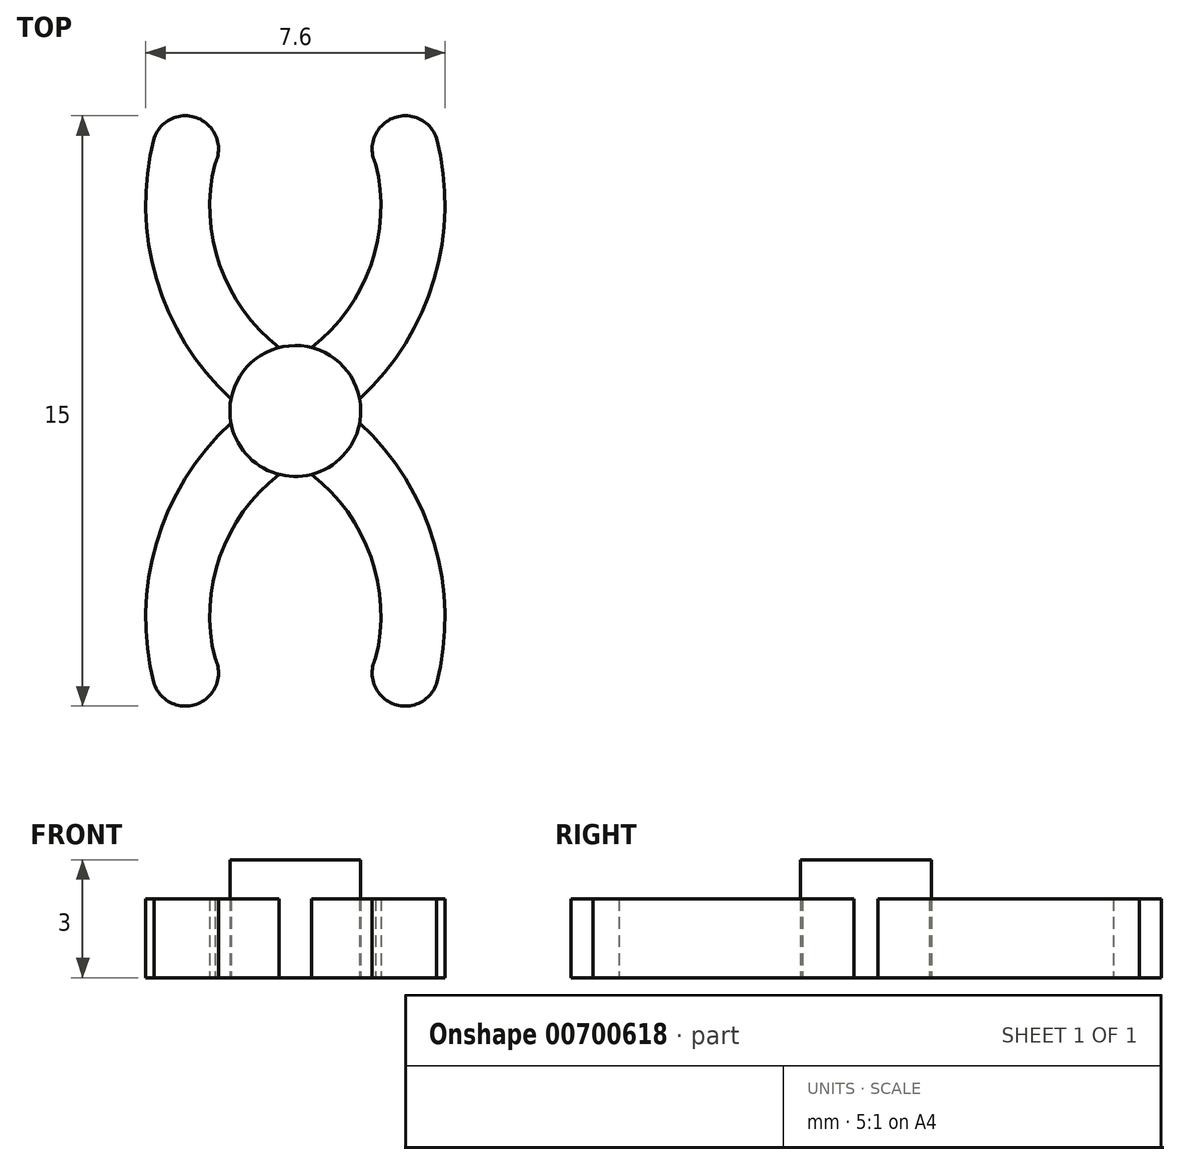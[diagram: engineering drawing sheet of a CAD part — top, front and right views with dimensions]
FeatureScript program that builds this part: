
annotation { "Feature Type Name" : "Feature", "Feature Type Description" : "" }
export const myFeature = defineFeature(function(context is Context, id is Id, definition is map)
    precondition{}
    {
        {
            var Q0;
            Q0=qCreatedBy(makeId("Top.planeOp"),FACE);
            var sketch = newSketch(context, id + "F0", { "sketchPlane" : qUnion([Q0])});
            skLineSegment(sketch, "E0", {"start": v(-1.04, 1.33) * mm, "end": v(-1.04, -7.3) * mm, "construction": true});
            skArc(sketch, "E1", {"start": v(-1.04, 1.33) * mm, "mid": v(0.79, 3.47) * mm, "end": v(1, 6.28) * mm});
            skLineSegment(sketch, "E2", {"start": v(1, 6.28) * mm, "end": v(6, 6.28) * mm, "construction": true});
            skLineSegment(sketch, "E3", {"start": v(1, 6.28) * mm, "end": v(4.09, 7.6) * mm, "construction": true});
            skArc(sketch, "E4", {"start": v(2.54, 6.94) * mm, "mid": v(1.42, 7.43) * mm, "end": v(1, 6.28) * mm});
            skArc(sketch, "E5", {"start": v(0.24, 0) * mm, "mid": v(2.42, 3.13) * mm, "end": v(2.54, 6.94) * mm});
            skArc(sketch, "E6.MirrorCS", {"start": v(-1.04, -1.33) * mm, "mid": v(0.79, -3.47) * mm, "end": v(1, -6.28) * mm});
            skArc(sketch, "E7.MirrorCS", {"start": v(2.54, -6.94) * mm, "mid": v(1.42, -7.43) * mm, "end": v(1, -6.28) * mm});
            skArc(sketch, "E8.MirrorCS", {"start": v(0.24, 0) * mm, "mid": v(2.42, -3.13) * mm, "end": v(2.54, -6.94) * mm});
            skArc(sketch, "E9.MirrorCS", {"start": v(-1.04, -1.33) * mm, "mid": v(-2.87, -3.47) * mm, "end": v(-3.08, -6.28) * mm});
            skArc(sketch, "E10.MirrorCS", {"start": v(-1.04, 1.33) * mm, "mid": v(-2.87, 3.47) * mm, "end": v(-3.08, 6.28) * mm});
            skArc(sketch, "E11.MirrorCS", {"start": v(-2.32, 0) * mm, "mid": v(-4.5, -3.13) * mm, "end": v(-4.63, -6.94) * mm});
            skArc(sketch, "E12.MirrorCS", {"start": v(-2.32, 0) * mm, "mid": v(-4.5, 3.13) * mm, "end": v(-4.63, 6.94) * mm});
            skArc(sketch, "E13.MirrorCS", {"start": v(-4.63, -6.94) * mm, "mid": v(-3.5, -7.43) * mm, "end": v(-3.08, -6.28) * mm});
            skArc(sketch, "E14.MirrorCS", {"start": v(-4.63, 6.94) * mm, "mid": v(-3.5, 7.43) * mm, "end": v(-3.08, 6.28) * mm});
            skSolve(sketch);
        }
        {
            var Q0;
            Q0=makeQuery(id+"F0.imprint","IMPRINT",FACE,{"disambiguationData":[TD([[makeQuery(id+"F0.imprint","IMPRINT",EDGE,{"derivedFrom":sQuery(id+"F0.wireOp",EDGE,"E1")}),-1.0]])]});
            extrude(context, id + "F1", {"entities" : qUnion([Q0]), "depth" : 2 * mm, "offsetDistance" : 25.4 * mm});
        }
        {
            var Q0;
            Q0=makeQuery(id+"F1.opExtrude","CAP_FACE",FACE,{"disambiguationData":[OSD([sQuery(id+"F0.wireOp",EDGE,"E1"),sQuery(id+"F0.wireOp",EDGE,"E4"),sQuery(id+"F0.wireOp",EDGE,"E5"),sQuery(id+"F0.wireOp",EDGE,"E6.MirrorCS"),sQuery(id+"F0.wireOp",EDGE,"E7.MirrorCS"),sQuery(id+"F0.wireOp",EDGE,"E8.MirrorCS"),sQuery(id+"F0.wireOp",EDGE,"E9.MirrorCS"),sQuery(id+"F0.wireOp",EDGE,"E10.MirrorCS"),sQuery(id+"F0.wireOp",EDGE,"E11.MirrorCS"),sQuery(id+"F0.wireOp",EDGE,"E12.MirrorCS"),sQuery(id+"F0.wireOp",EDGE,"E13.MirrorCS"),sQuery(id+"F0.wireOp",EDGE,"E14.MirrorCS")])],"isStart":false});
            var sketch = newSketch(context, id + "F2", { "sketchPlane" : qUnion([Q0])});
            skLineSegment(sketch, "E15", {"start": v(-1.04, 1.33) * mm, "end": v(-1.04, -1.33) * mm, "construction": true});
            skLineSegment(sketch, "E16", {"start": v(-2.32, 0) * mm, "end": v(0.24, 0) * mm, "construction": true});
            skCircle(sketch, "E17", {"center": v(-1.04, 0) * mm, "radius": 1.66 * mm});
            skSolve(sketch);
        }
        {
            var Q0;
            Q0 = qSketchRegion(id + "F2", true);
            extrude(context, id + "F3", {"entities" : qUnion([Q0]), "operationType" : NewBodyOperationType.ADD, "depth" : 1 * mm, "offsetDistance" : 25.4 * mm, "hasSecondDirection" : true, "secondDirectionOppositeDirection" : true, "secondDirectionDepth" : 2 * mm});
        }
    });
